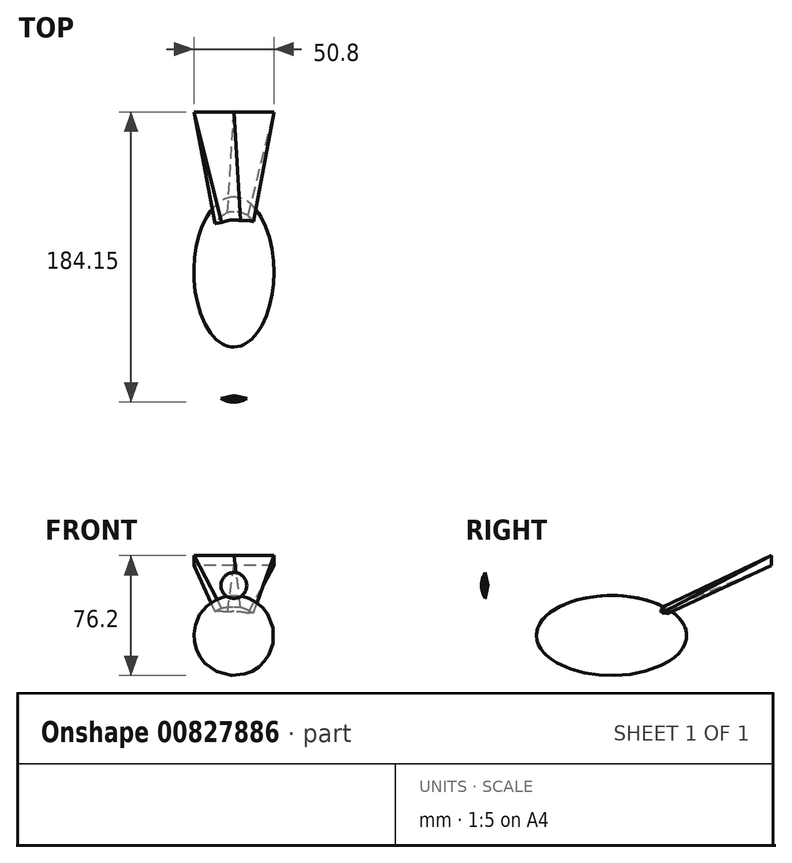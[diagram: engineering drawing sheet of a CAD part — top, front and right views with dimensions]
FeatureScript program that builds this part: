
annotation { "Feature Type Name" : "Feature", "Feature Type Description" : "" }
export const myFeature = defineFeature(function(context is Context, id is Id, definition is map)
    precondition{}
    {
        {
            var Q0;
            Q0=qCreatedBy(makeId("Right.planeOp"),FACE);
            var sketch = newSketch(context, id + "F0", { "sketchPlane" : qUnion([Q0])});
            skEllipse(sketch, "E0", {"center": v(0, 0) * mm, "majorRadius": 47.63 * mm, "minorRadius": 25.4 * mm, "majorAxis": v(-1, 0)});
            skLineSegment(sketch, "E1", {"start": v(47.63, 0) * mm, "end": v(-47.63, 0) * mm});
            skLineSegment(sketch, "E2", {"start": v(-47.63, 0) * mm, "end": v(-66.68, 0) * mm});
            skLineSegment(sketch, "E3", {"start": v(-66.68, 0) * mm, "end": v(-66.68, 31.75) * mm});
            skCircle(sketch, "E4", {"center": v(-66.68, 31.75) * mm, "radius": 15.88 * mm});
            skLineSegment(sketch, "E5", {"start": v(-66.68, 31.75) * mm, "end": v(-50.8, 31.75) * mm});
            skLineSegment(sketch, "E6", {"start": v(-50.8, 31.75) * mm, "end": v(-82.55, 31.75) * mm});
            skLineSegment(sketch, "E7", {"start": v(-82.55, 22.86) * mm, "end": v(-94.73, 19.28) * mm});
            skLineSegment(sketch, "E8", {"start": v(-94.73, 19.28) * mm, "end": v(-82.55, 31.75) * mm});
            skLineSegment(sketch, "E9", {"start": v(-94.73, 19.28) * mm, "end": v(-80.26, 23.53) * mm});
            skLineSegment(sketch, "E10", {"start": v(-80.26, 23.53) * mm, "end": v(-78.5, 31.75) * mm});
            skLineSegment(sketch, "E11", {"start": v(-78.5, 31.75) * mm, "end": v(-82.55, 31.75) * mm});
            skSolve(sketch);
        }
        {
            var Q0;
            {var subQ0=sQuery(id+"F0.wireOp",EDGE,"E1");Q0=makeQuery(id+"F0.imprint","IMPRINT",FACE,{"disambiguationData":[TD([[makeQuery(id+"F0.imprint","IMPRINT",EDGE,{"derivedFrom":subQ0}),-1.0]])]});}
            var Q1;
            Q1=sQuery(id+"F0.wireOp",EDGE,"E1");
            revolve(context, id + "F1", {"surfaceOperationType" : NewSurfaceOperationType.NEW, "entities" : qUnion([Q0]), "axis" : qUnion([Q1]), "revolveType" : RevolveType.FULL});
        }
        {
            var Q0;
            {var subQ0=sQuery(id+"F0.wireOp",EDGE,"E6");var subQ1=sQuery(id+"F0.wireOp",EDGE,"E4");var subQ2=makeQuery(id+"F0.imprint","INTERSECT",VERTEX,{"disambiguationData":[OD(0.0)],"derivedFrom":[subQ1,subQ0]});Q0=makeQuery(id+"F0.imprint","IMPRINT",FACE,{"disambiguationData":[TD([[makeQuery(id+"F0.imprint","IMPRINT",EDGE,{"disambiguationData":[TD([[subQ2,-1.0]])],"derivedFrom":subQ1}),1.0]])]});}
            var Q1;
            Q1=sQuery(id+"F0.wireOp",EDGE,"E6");
            revolve(context, id + "F2", {"surfaceOperationType" : NewSurfaceOperationType.NEW, "entities" : qUnion([Q0]), "axis" : qUnion([Q1]), "revolveType" : RevolveType.FULL});
        }
        {
            var Q0;
            Q0=qCreatedBy(makeId("Front.planeOp"),FACE);
            cPlane(context, id + "F3", {"entities" : qUnion([Q0]), "cplaneType" : CPlaneType.OFFSET, "offset" : 101.6 * mm, "oppositeDirection" : true, "width" : 152.4 * mm, "height" : 152.4 * mm});
        }
        {
            var Q0;
            Q0=qCreatedBy(id+"F3.planeOp",FACE);
            var sketch = newSketch(context, id + "F4", { "sketchPlane" : qUnion([Q0])});
            skLineSegment(sketch, "E12", {"start": v(0, 0) * mm, "end": v(0, 50.8) * mm});
            skLineSegment(sketch, "E13", {"start": v(0, 50.8) * mm, "end": v(-25.4, 50.8) * mm});
            skLineSegment(sketch, "E14", {"start": v(0, 50.8) * mm, "end": v(25.4, 50.8) * mm});
            skLineSegment(sketch, "E15.bottom", {"start": v(25.4, 50.8) * mm, "end": v(-25.4, 50.8) * mm});
            skLineSegment(sketch, "E15.top", {"start": v(25.4, 44.45) * mm, "end": v(-25.4, 44.45) * mm});
            skLineSegment(sketch, "E15.left", {"start": v(25.4, 50.8) * mm, "end": v(25.4, 44.45) * mm});
            skLineSegment(sketch, "E15.right", {"start": v(-25.4, 50.8) * mm, "end": v(-25.4, 44.45) * mm});
            skSolve(sketch);
        }
        {
            var Q0;
            Q0=qCreatedBy(makeId("Front.planeOp"),FACE);
            var sketch = newSketch(context, id + "F5", { "sketchPlane" : qUnion([Q0])});
            skLineSegment(sketch, "E16.bottom", {"start": v(-6.35, -2.54) * mm, "end": v(6.35, -2.54) * mm});
            skLineSegment(sketch, "E16.top", {"start": v(-6.35, 2.54) * mm, "end": v(6.35, 2.54) * mm});
            skLineSegment(sketch, "E16.left", {"start": v(-6.35, -2.54) * mm, "end": v(-6.35, 2.54) * mm});
            skLineSegment(sketch, "E16.right", {"start": v(6.35, -2.54) * mm, "end": v(6.35, 2.54) * mm});
            skPoint(sketch, "E16.middle", {"position": v(0, 0) * mm});
            skSolve(sketch);
        }
        {
            var Q1;
            Q1 = qSketchRegion(id + "F5", true);
            var Q2;
            {var subQ0=sQuery(id+"F4.wireOp",EDGE,"E14");var subQ1=sQuery(id+"F4.wireOp",EDGE,"E13");Q2=qUnion([makeQuery(id+"F4.imprint","IMPRINT",FACE,{"disambiguationData":[TD([[makeQuery(id+"F4.imprint","IMPRINT",EDGE,{"derivedFrom":subQ1}),1.0]])]}),makeQuery(id+"F4.imprint","IMPRINT",FACE,{"disambiguationData":[TD([[makeQuery(id+"F4.imprint","IMPRINT",EDGE,{"derivedFrom":subQ0}),-1.0]])]})]);}
            loft(context, id + "F6", {"operationType" : NewBodyOperationType.ADD, "sheetProfilesArray" : [{ "sheetProfileEntities" : qUnion([Q1]) }, { "sheetProfileEntities" : qUnion([Q2]) }]});
        }
    });
